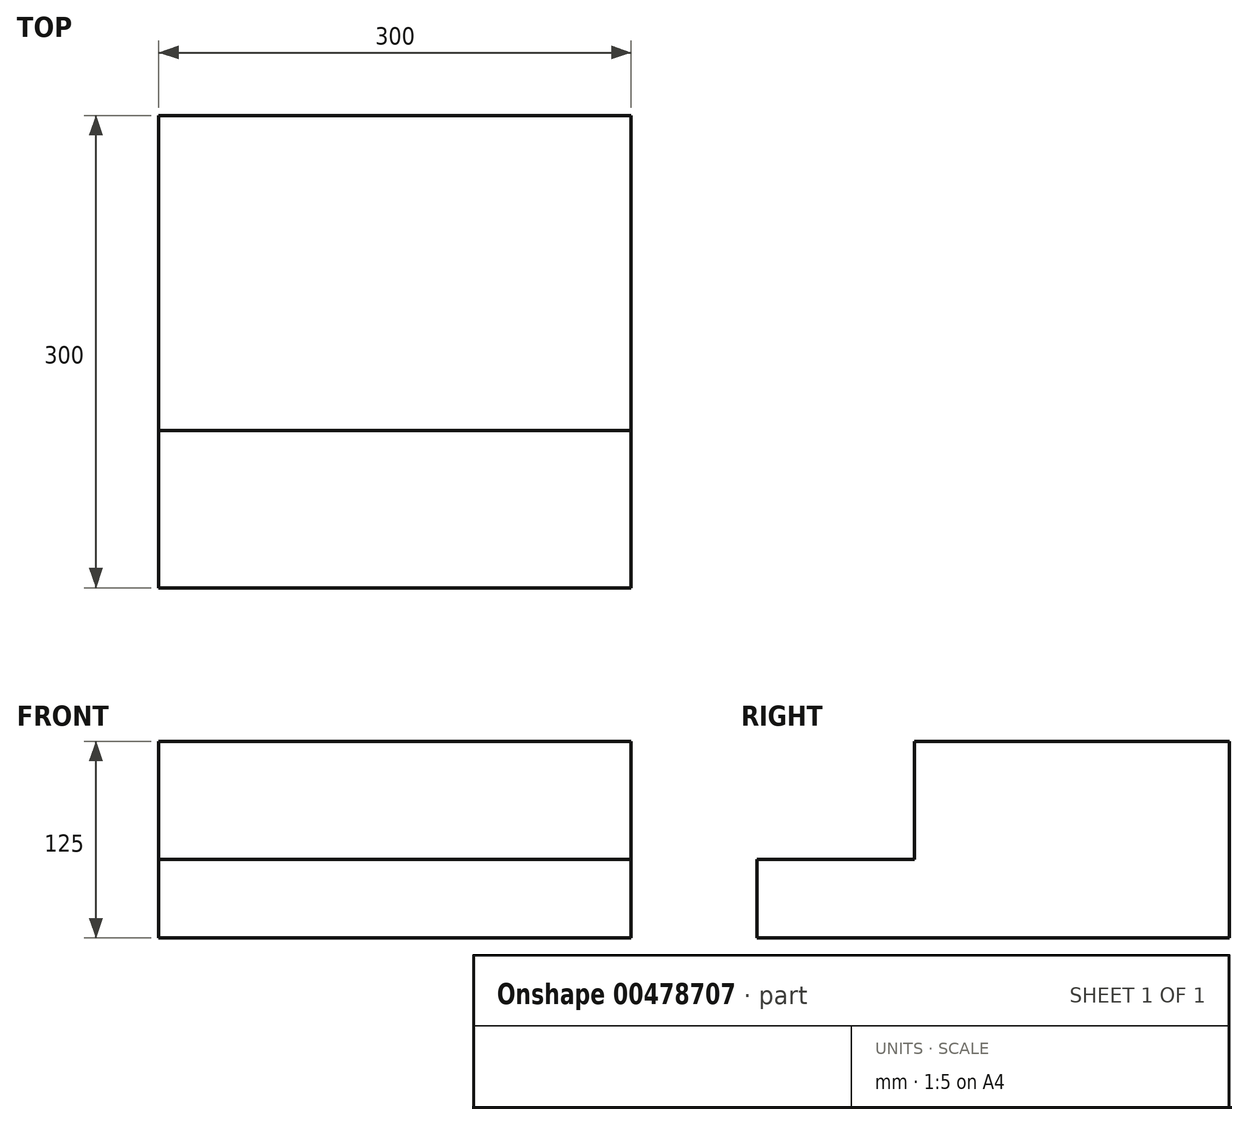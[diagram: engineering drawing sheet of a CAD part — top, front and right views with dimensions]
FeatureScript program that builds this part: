
annotation { "Feature Type Name" : "Feature", "Feature Type Description" : "" }
export const myFeature = defineFeature(function(context is Context, id is Id, definition is map)
    precondition{}
    {
        {
            var Q0;
            Q0=qCreatedBy(makeId("Top.planeOp"),FACE);
            var sketch = newSketch(context, id + "F0", { "sketchPlane" : qUnion([Q0])});
            skLineSegment(sketch, "E0", {"start": v(-300, 126.16) * mm, "end": v(-300, -173.84) * mm});
            skLineSegment(sketch, "E1", {"start": v(-300, 126.16) * mm, "end": v(0, 126.16) * mm});
            skLineSegment(sketch, "E2", {"start": v(0, 126.16) * mm, "end": v(0, -173.84) * mm});
            skLineSegment(sketch, "E3", {"start": v(0, -173.84) * mm, "end": v(-300, -173.84) * mm});
            skSolve(sketch);
        }
        {
            var Q0;
            Q0=makeQuery(id+"F0.imprint","IMPRINT",FACE,{"disambiguationData":[TD([[makeQuery(id+"F0.imprint","IMPRINT",EDGE,{"derivedFrom":sQuery(id+"F0.wireOp",EDGE,"E0")}),1.0]])]});
            extrude(context, id + "F1", {"entities" : qUnion([Q0]), "depth" : 125 * mm});
        }
        {
            var Q0;
            Q0=makeQuery(id+"F1.opExtrude","CAP_FACE",FACE,{"disambiguationData":[OSD([sQuery(id+"F0.wireOp",EDGE,"E0"),sQuery(id+"F0.wireOp",EDGE,"E1"),sQuery(id+"F0.wireOp",EDGE,"E2"),sQuery(id+"F0.wireOp",EDGE,"E3")])],"isStart":false});
            var sketch = newSketch(context, id + "F2", { "sketchPlane" : qUnion([Q0])});
            skLineSegment(sketch, "E4", {"start": v(0, -173.84) * mm, "end": v(0, -73.84) * mm});
            skLineSegment(sketch, "E5", {"start": v(0, -73.84) * mm, "end": v(-300, -73.84) * mm});
            skLineSegment(sketch, "E6", {"start": v(-300, -73.84) * mm, "end": v(-300, -173.84) * mm});
            skLineSegment(sketch, "E7", {"start": v(-300, -173.84) * mm, "end": v(0, -173.84) * mm});
            skSolve(sketch);
        }
        {
            var Q0;
            Q0=qSketchRegion(id+"F2",true);
            extrude(context, id + "F3", {"entities" : qUnion([Q0]), "operationType" : NewBodyOperationType.REMOVE, "oppositeDirection" : true, "depth" : 75 * mm});
        }
    });
